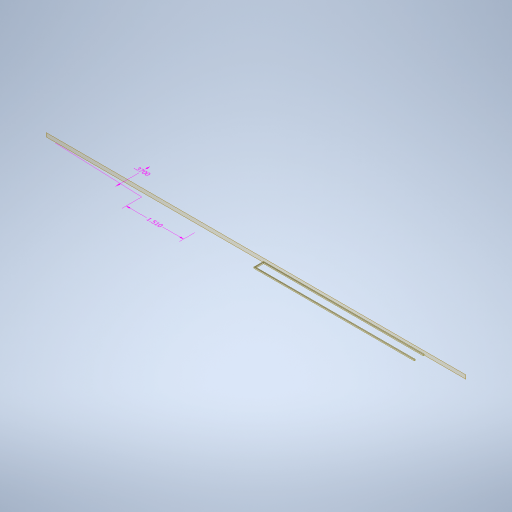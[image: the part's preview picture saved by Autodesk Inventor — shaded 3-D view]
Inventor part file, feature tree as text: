
AUTODESK INVENTOR PART (.ipt)
format: ipt  version: 2024.2 (Build 282272000, 272)  size: 275,968 bytes
history: native  units: in
note: dims shown in document units (in); Inventor stores cm internally (conversion verified against a paired STEP export)
features: other x3, plane x3, sketch x2, sweep x1
ambient origin geometry x8: Origin, YZ Plane, XZ Plane, XY Plane, X Axis, Y Axis, Z Axis, Center Point
bodies: Solid1 (feature_tree)
feature tree (9):
  other  "Annotations"
  sweep  "Sweep1"
  plane  "Work Plane1"
  plane  "Work Plane2"
  plane  "Work Plane4"
  sketch  "Sketch1"  dims[d6=0.0in d7=0.0in d11=0.25in d19=-0.25in]
  sketch  "Sketch2"  dims[d69=1.625in d70=1.625in d86=-0.1175in d89=0.1in d90=0.0in d91=0.0in d92=0.0in d98=0.01in d99=0.01in d42=0.2341in d43=0.169in d44=0.37in d48=0.2141in d49=0.2512in d50=1.51in]
  other  "Linear Dimension 1"
  other  "Linear Dimension 3"
